# Revit family: AFX-Metropolitan-Sconce_
name_source: partatom
category: Lighting Fixtures
units: mm (PartAtom-declared; Revit-internal decimal feet)

## family parameters
Cut with Voids When Loaded = No
Host = Face
Light Source = Yes
Maintain Annotation Orientation = No
Part Type = Normal
Room Calculation Point = No
Round Connector Dimension = Use Diameter
Shared = No

## types (1)
- METS0512
    Apparent Load = 0 VA
    Assembly Code = D5020200
    Canopy Finish = AFX - Paint Black
    Cap Finish = AFX - Plastic Black
    Color Filter = 16777215
    Default Elevation = 48"
    Depth = 7 3/8"
    Description = LED Sconce - 5"W x 7 3/8"D x 12"H
    Diffuser Finish = AFX - Diffuser
    Dimming Lamp Color Temperature Shift = <None>
    Emit Shape Visible in Rendering = No
    Emit from Circle Diameter = 5"
    Height = 12"
    Keynote = 12500
    Manufacturer = AFX Inc
    Model = METS0512
    Photometric Web File = METS0512LxxD1xx.IES
    Power Factor = 1
    Product Documentation Link = https://www.afxinc.com
    Revit Model Built By = https://www.servex-us.com
    Support Finish = AFX - Paint Black
    Sustainability = https://lamprecycle.org
    Tilt Angle = 90.00°
    Type Comments = Metropolitan
    URL = https://www.afxinc.com
    Voltage = 12 V
    Wattage Comments = 10W
    Width = 5"

## geometry (parser evidence)
native form markers: Sweep x5
no freeform markers — native parametric forms only
